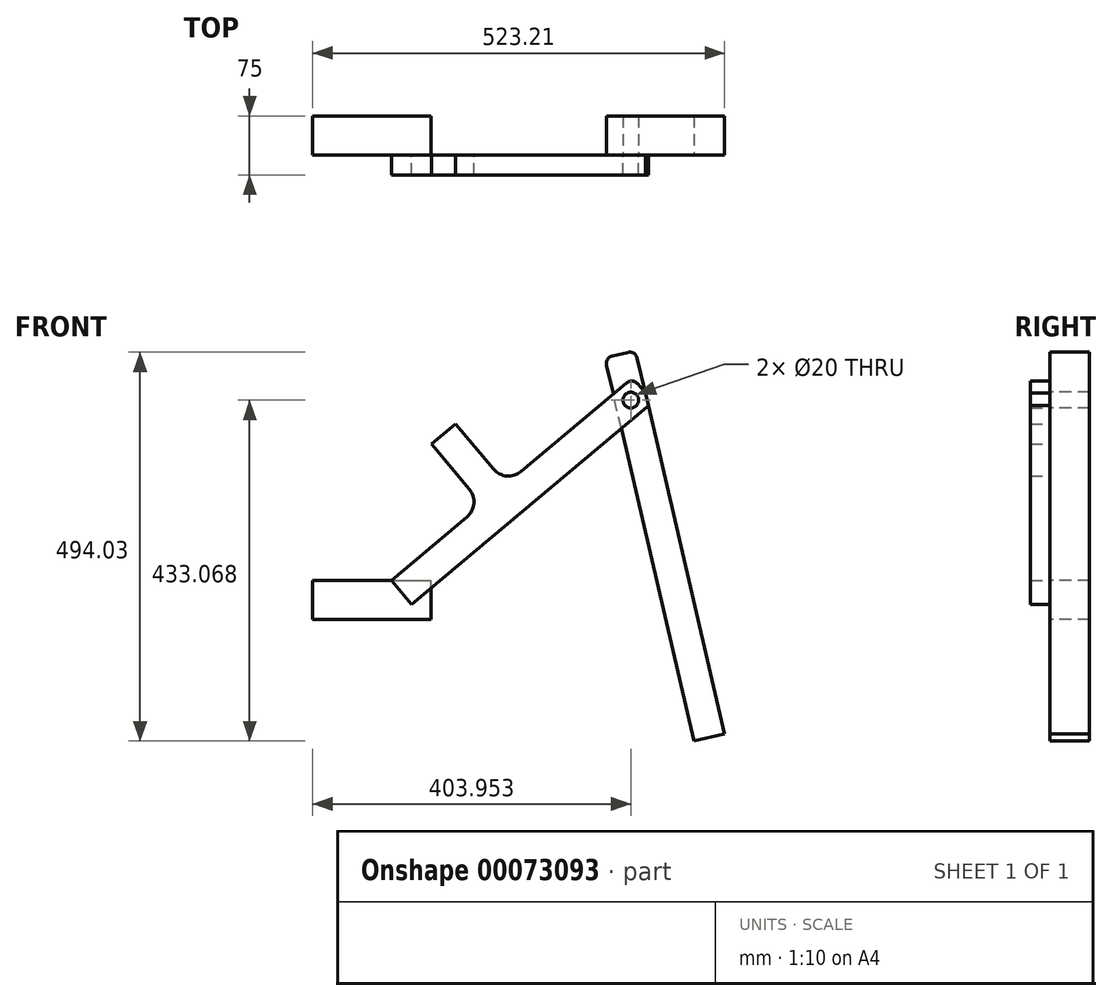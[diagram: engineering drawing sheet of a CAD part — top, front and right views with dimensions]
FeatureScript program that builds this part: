
annotation { "Feature Type Name" : "Feature", "Feature Type Description" : "" }
export const myFeature = defineFeature(function(context is Context, id is Id, definition is map)
    precondition{}
    {
        {
            var Q0;
            Q0=qCreatedBy(makeId("Front.planeOp"),FACE);
            cPlane(context, id + "F0", {"entities" : qUnion([Q0]), "cplaneType" : CPlaneType.OFFSET, "offset" : 25 * mm, "width" : 150 * mm, "height" : 150 * mm});
        }
        {
            var Q0;
            Q0=qCreatedBy(id+"F0.planeOp",FACE);
            var sketch = newSketch(context, id + "F1", { "sketchPlane" : qUnion([Q0])});
            skLineSegment(sketch, "E0.bottom", {"start": v(-100, -50) * mm, "end": v(50, -50) * mm});
            skLineSegment(sketch, "E0.top", {"start": v(-100, 0) * mm, "end": v(50, 0) * mm});
            skLineSegment(sketch, "E0.left", {"start": v(-100, -50) * mm, "end": v(-100, 0) * mm});
            skLineSegment(sketch, "E0.right", {"start": v(50, -50) * mm, "end": v(50, 0) * mm});
            skLineSegment(sketch, "E1", {"start": v(0, 0) * mm, "end": v(95.76, 80.35) * mm});
            skLineSegment(sketch, "E2", {"start": v(312.85, 249.45) * mm, "end": v(325.7, 234.13) * mm});
            skLineSegment(sketch, "E3", {"start": v(324.47, 220.05) * mm, "end": v(25.71, -30.64) * mm});
            skLineSegment(sketch, "E4", {"start": v(25.71, -30.64) * mm, "end": v(0, 0) * mm});
            skLineSegment(sketch, "E5", {"start": v(98.84, 115.57) * mm, "end": v(50.63, 173.02) * mm});
            skLineSegment(sketch, "E6", {"start": v(50.63, 173.02) * mm, "end": v(81.27, 198.73) * mm});
            skLineSegment(sketch, "E7", {"start": v(81.27, 198.73) * mm, "end": v(129.48, 141.28) * mm});
            skLineSegment(sketch, "E8", {"start": v(312.1, 282.17) * mm, "end": v(423.2, -195.06) * mm});
            skLineSegment(sketch, "E9", {"start": v(423.2, -195.06) * mm, "end": v(384.25, -204.13) * mm});
            skLineSegment(sketch, "E10", {"start": v(384.25, -204.13) * mm, "end": v(273.14, 273.1) * mm});
            skLineSegment(sketch, "E11", {"start": v(280.6, 285.1) * mm, "end": v(300.09, 289.64) * mm});
            skLineSegment(sketch, "E12", {"start": v(319.27, 241.8) * mm, "end": v(303.95, 228.94) * mm, "construction": true});
            skCircle(sketch, "E13", {"center": v(303.95, 228.94) * mm, "radius": 10 * mm});
            skLineSegment(sketch, "E14", {"start": v(290.35, 287.38) * mm, "end": v(303.95, 228.94) * mm, "construction": true});
            skPoint(sketch, "E15.visualSharp", {"position": v(270.87, 282.84) * mm});
            skArc(sketch, "E15.filletArc", {"start": v(280.6, 285.1) * mm, "mid": v(274.38, 280.65) * mm, "end": v(273.14, 273.1) * mm});
            skPoint(sketch, "E16.visualSharp", {"position": v(309.83, 291.91) * mm});
            skArc(sketch, "E16.filletArc", {"start": v(312.1, 282.17) * mm, "mid": v(307.64, 288.4) * mm, "end": v(300.09, 289.64) * mm});
            skPoint(sketch, "E17.visualSharp", {"position": v(306.42, 257.12) * mm});
            skArc(sketch, "E17.filletArc", {"start": v(312.85, 249.45) * mm, "mid": v(306.06, 252.99) * mm, "end": v(298.76, 250.69) * mm});
            skPoint(sketch, "E18.visualSharp", {"position": v(332.13, 226.47) * mm});
            skArc(sketch, "E18.filletArc", {"start": v(324.47, 220.05) * mm, "mid": v(328, 226.83) * mm, "end": v(325.7, 234.13) * mm});
            skLineSegment(sketch, "E19.trimOffspring", {"start": v(164.7, 138.2) * mm, "end": v(298.76, 250.69) * mm});
            skPoint(sketch, "E20.visualSharp", {"position": v(145.55, 122.13) * mm});
            skArc(sketch, "E20.filletArc", {"start": v(129.48, 141.28) * mm, "mid": v(146.45, 132.45) * mm, "end": v(164.7, 138.2) * mm});
            skPoint(sketch, "E21.visualSharp", {"position": v(114.9, 96.42) * mm});
            skArc(sketch, "E21.filletArc", {"start": v(95.76, 80.35) * mm, "mid": v(104.6, 97.32) * mm, "end": v(98.84, 115.57) * mm});
            skSolve(sketch);
        }
        {
            var Q0;
            {var subQ1=sQuery(id+"F1.wireOp",EDGE,"E0.bottom");Q0=makeQuery(id+"F1.imprint","IMPRINT",FACE,{"disambiguationData":[TD([[makeQuery(id+"F1.imprint","IMPRINT",EDGE,{"derivedFrom":subQ1}),1.0]])]});}
            var Q1;
            {var subQ3=sQuery(id+"F1.wireOp",EDGE,"E4");Q1=makeQuery(id+"F1.imprint","IMPRINT",FACE,{"disambiguationData":[TD([[makeQuery(id+"F1.imprint","IMPRINT",EDGE,{"derivedFrom":subQ3}),-1.0]])]});}
            var Q2;
            {var subQ0=sQuery(id+"F1.wireOp",EDGE,"E9");Q2=makeQuery(id+"F1.imprint","IMPRINT",FACE,{"disambiguationData":[TD([[makeQuery(id+"F1.imprint","IMPRINT",EDGE,{"derivedFrom":subQ0}),-1.0]])]});}
            var Q3;
            Q3=makeQuery(id+"F1.imprint","IMPRINT",FACE,{"disambiguationData":[TD([[makeQuery(id+"F1.imprint","IMPRINT",EDGE,{"derivedFrom":sQuery(id+"F1.wireOp",EDGE,"E13")}),-1.0]])]});
            var Q4;
            Q4=makeQuery(id+"F1.imprint","IMPRINT",FACE,{"disambiguationData":[TD([[makeQuery(id+"F1.imprint","IMPRINT",EDGE,{"derivedFrom":sQuery(id+"F1.wireOp",EDGE,"E11")}),-1.0]])]});
            extrude(context, id + "F2", {"entities" : qUnion([Q0, Q1, Q2, Q3, Q4]), "oppositeDirection" : true, "depth" : 50 * mm});
        }
        {
            var Q0;
            {var subQ10=sQuery(id+"F1.wireOp",EDGE,"E1");Q0=makeQuery(id+"F1.imprint","IMPRINT",FACE,{"disambiguationData":[TD([[makeQuery(id+"F1.imprint","IMPRINT",EDGE,{"derivedFrom":subQ10}),-1.0]])]});}
            var Q1;
            Q1=makeQuery(id+"F1.imprint","IMPRINT",FACE,{"disambiguationData":[TD([[makeQuery(id+"F1.imprint","IMPRINT",EDGE,{"derivedFrom":sQuery(id+"F1.wireOp",EDGE,"E13")}),-1.0]])]});
            var Q2;
            {var subQ3=sQuery(id+"F1.wireOp",EDGE,"E4");Q2=makeQuery(id+"F1.imprint","IMPRINT",FACE,{"disambiguationData":[TD([[makeQuery(id+"F1.imprint","IMPRINT",EDGE,{"derivedFrom":subQ3}),-1.0]])]});}
            extrude(context, id + "F3", {"entities" : qUnion([Q0, Q1, Q2]), "depth" : 25 * mm});
        }
    });
